# Revit family: TP-Profil-FS
name_source: partatom
category: Generic Models
revit_build: Autodesk Revit 2017 (Build: 20160225_1515(x64)
units: mm (PartAtom-declared; Revit-internal decimal feet)

## family parameters
Always vertical = Yes
Can host rebar = No
Cut with Voids When Loaded = No
Part Type = Normal
Room Calculation Point = No
Round Connector Dimension = Use Diameter
Shared = No
Work Plane-Based = No

## types (2) — shared parameters
Cut's number = 29
Cut's number 2 = 2
Cut's number 3 = 58
Cut's space = 100 mm  [stored 0.328084 ft]
Cut's space 2 = 50 mm  [stored 0.164042 ft]
Length = 2900 mm
Manufacturer = OBO BETTERMANN
URL = http://www.obo-bettermann.com

## per-type parameters (varying)
| type | GTIN | Manufacturer Art.No. | Material |
| TPSG 3000 FS | 4012196079032 | 6366090 | Strip-galvanised |
| TPSG 3000 FT | 4012195424925 | 6366093 | Hot-dip galvanised |

note: column(s) folded — value = type name in every type: Article Type

note: [stored X ft] marks values corroborated as IEEE doubles in the binary element streams (Revit-internal decimal feet)

## geometry (parser evidence)
native form markers: Sweep x2
no freeform markers — native parametric forms only
